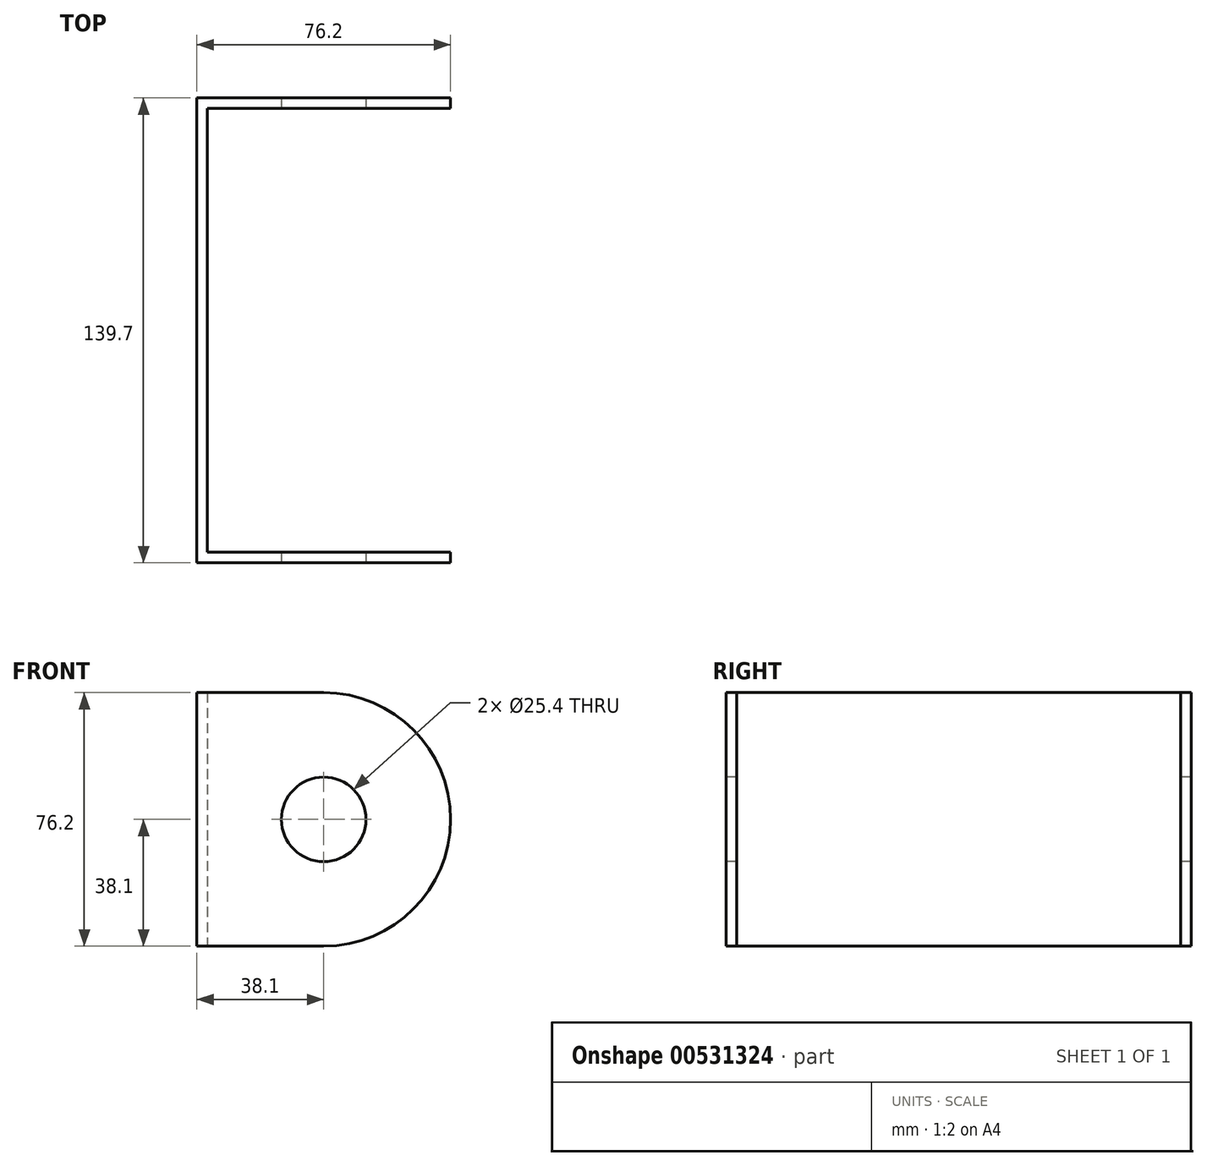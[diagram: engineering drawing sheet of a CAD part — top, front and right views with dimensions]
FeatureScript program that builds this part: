
annotation { "Feature Type Name" : "Feature", "Feature Type Description" : "" }
export const myFeature = defineFeature(function(context is Context, id is Id, definition is map)
    precondition{}
    {
        {
            var Q0;
            Q0=qCreatedBy(makeId("Right.planeOp"),FACE);
            var sketch = newSketch(context, id + "F0", { "sketchPlane" : qUnion([Q0])});
            skLineSegment(sketch, "E0.bottom", {"start": v(-69.85, 38.1) * mm, "end": v(69.85, 38.1) * mm});
            skLineSegment(sketch, "E0.top", {"start": v(-69.85, -38.1) * mm, "end": v(69.85, -38.1) * mm});
            skLineSegment(sketch, "E0.left", {"start": v(-69.85, 38.1) * mm, "end": v(-69.85, -38.1) * mm});
            skLineSegment(sketch, "E0.right", {"start": v(69.85, 38.1) * mm, "end": v(69.85, -38.1) * mm});
            skPoint(sketch, "E0.middle", {"position": v(0, 0) * mm});
            skSolve(sketch);
        }
        {
            var Q0;
            Q0=makeQuery(id+"F0.imprint","IMPRINT",FACE,{"disambiguationData":[TD([[makeQuery(id+"F0.imprint","IMPRINT",EDGE,{"derivedFrom":sQuery(id+"F0.wireOp",EDGE,"E0.bottom")}),-1.0]])]});
            extrude(context, id + "F1", {"entities" : qUnion([Q0]), "depth" : 76.2 * mm, "offsetDistance" : 25.4 * mm});
        }
        {
            var Q0;
            Q0=makeQuery(id+"F1.opExtrude","CAP_FACE",FACE,{"disambiguationData":[OSD([sQuery(id+"F0.wireOp",EDGE,"E0.bottom"),sQuery(id+"F0.wireOp",EDGE,"E0.top"),sQuery(id+"F0.wireOp",EDGE,"E0.left"),sQuery(id+"F0.wireOp",EDGE,"E0.right")])],"isStart":false});
            var sketch = newSketch(context, id + "F2", { "sketchPlane" : qUnion([Q0])});
            skLineSegment(sketch, "E1.bottom", {"start": v(-66.67, 38.1) * mm, "end": v(66.67, 38.1) * mm});
            skLineSegment(sketch, "E1.top", {"start": v(-66.68, -38.1) * mm, "end": v(66.68, -38.1) * mm});
            skLineSegment(sketch, "E1.left", {"start": v(-66.67, 38.1) * mm, "end": v(-66.68, -38.1) * mm});
            skLineSegment(sketch, "E1.right", {"start": v(66.68, 38.1) * mm, "end": v(66.67, -38.1) * mm});
            skLineSegment(sketch, "E2", {"start": v(0, 38.1) * mm, "end": v(0, -38.1) * mm, "construction": true});
            skSolve(sketch);
        }
        {
            var Q0;
            Q0=makeQuery(id+"F2.imprint","IMPRINT",FACE,{"disambiguationData":[TD([[makeQuery(id+"F2.imprint","IMPRINT",EDGE,{"derivedFrom":sQuery(id+"F2.wireOp",EDGE,"E1.bottom")}),-1.0]])]});
            extrude(context, id + "F3", {"entities" : qUnion([Q0]), "operationType" : NewBodyOperationType.REMOVE, "oppositeDirection" : true, "depth" : 73.02 * mm, "offsetDistance" : 25.4 * mm});
        }
        {
            var Q0;
            Q0=makeQuery(id+"F1.opExtrude","SWEPT_FACE",FACE,{"disambiguationData":[OSD([sQuery(id+"F0.wireOp",EDGE,"E0.left")])]});
            var sketch = newSketch(context, id + "F4", { "sketchPlane" : qUnion([Q0])});
            skPoint(sketch, "E3", {"position": v(38.1, 0) * mm});
            skPoint(sketch, "E3.positionSnap0", {"position": v(38.1, 38.1) * mm});
            skPoint(sketch, "E3.positionSnap1", {"position": v(76.2, 0) * mm});
            skPoint(sketch, "E4", {"position": v(76.2, 38.1) * mm});
            skPoint(sketch, "E5", {"position": v(76.2, -38.1) * mm});
            skPoint(sketch, "E6", {"position": v(0, -38.1) * mm});
            skPoint(sketch, "E7", {"position": v(0, 38.1) * mm});
            skCircle(sketch, "E8", {"center": v(38.1, 0) * mm, "radius": 12.7 * mm});
            skPoint(sketch, "E9", {"position": v(38.1, -38.1) * mm});
            skArc(sketch, "E10", {"start": v(38.1, -38.1) * mm, "mid": v(76.2, 0) * mm, "end": v(38.1, 38.1) * mm});
            skSolve(sketch);
        }
        {
            var Q0;
            {var subQ0=sQuery(id+"F4.wireOp",EDGE,"E10");var subQ1=sQuery(id+"F0.wireOp",EDGE,"E0.left");var subQ4=makeQuery(id+"F1.opExtrude","CAP_EDGE",EDGE,{"disambiguationData":[OSD([subQ1])],"isStart":false});var subQ5=makeQuery(id+"F4.imprint","INTERSECT",VERTEX,{"derivedFrom":[subQ4,subQ0]});Q0=makeQuery(id+"F4.imprint","IMPRINT",FACE,{"disambiguationData":[TD([[makeQuery(id+"F4.imprint","IMPRINT",EDGE,{"disambiguationData":[TD([[subQ5,-1.0]])],"derivedFrom":subQ0}),-1.0]])]});}
            var Q1;
            {var subQ0=sQuery(id+"F4.wireOp",EDGE,"E10");var subQ1=sQuery(id+"F0.wireOp",EDGE,"E0.left");var subQ4=makeQuery(id+"F1.opExtrude","CAP_EDGE",EDGE,{"disambiguationData":[OSD([subQ1])],"isStart":false});var subQ5=makeQuery(id+"F4.imprint","INTERSECT",VERTEX,{"derivedFrom":[subQ4,subQ0]});Q1=makeQuery(id+"F4.imprint","IMPRINT",FACE,{"disambiguationData":[TD([[makeQuery(id+"F4.imprint","IMPRINT",EDGE,{"disambiguationData":[TD([[subQ5,1.0]])],"derivedFrom":subQ0}),-1.0]])]});}
            var Q2;
            Q2=makeQuery(id+"F4.imprint","IMPRINT",FACE,{"disambiguationData":[TD([[makeQuery(id+"F4.imprint","IMPRINT",EDGE,{"derivedFrom":sQuery(id+"F4.wireOp",EDGE,"E8")}),1.0]])]});
            extrude(context, id + "F5", {"entities" : qUnion([Q0, Q1, Q2]), "operationType" : NewBodyOperationType.REMOVE, "oppositeDirection" : true, "depth" : 171.2 * mm, "offsetDistance" : 25.4 * mm});
        }
    });
